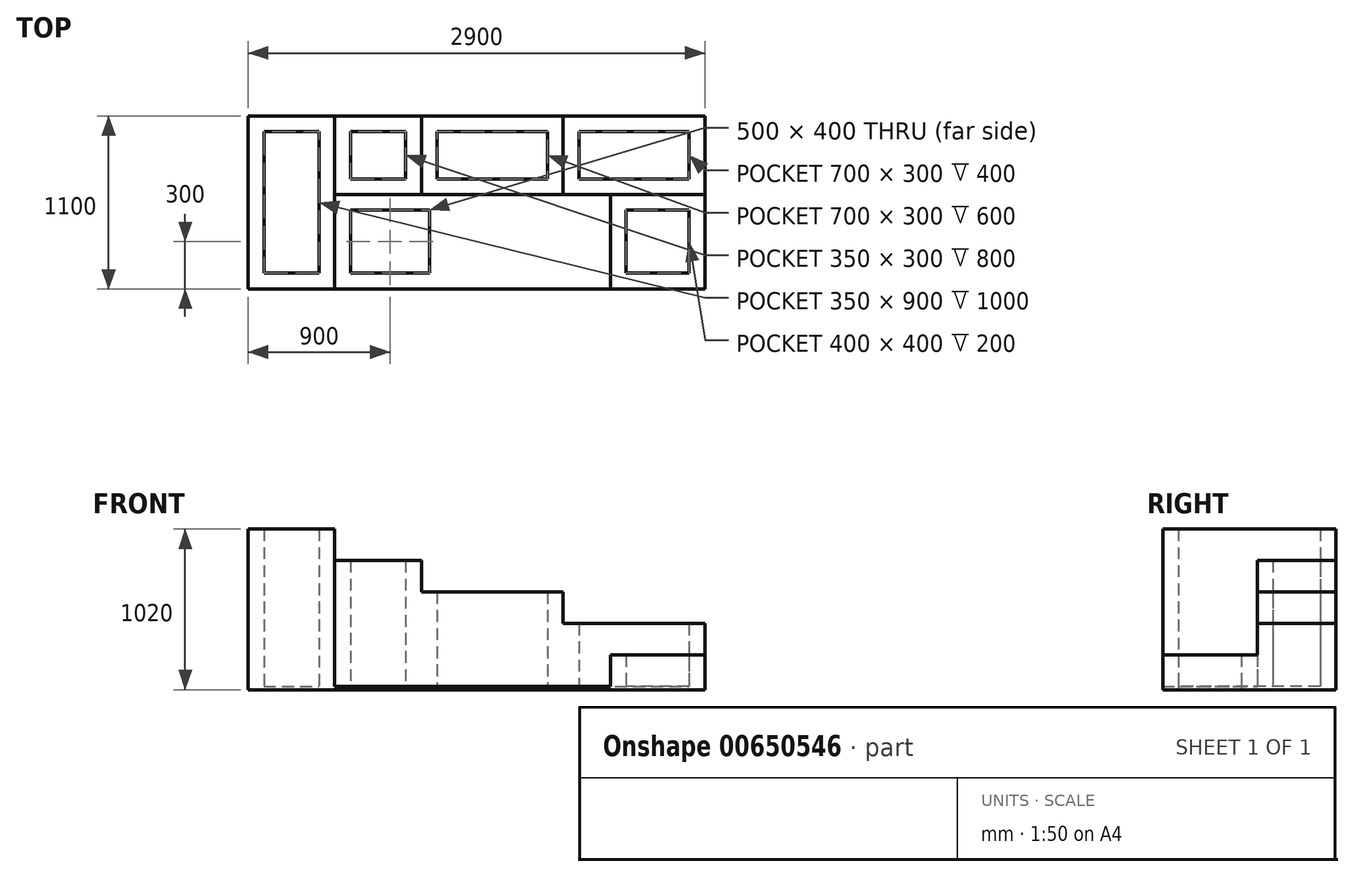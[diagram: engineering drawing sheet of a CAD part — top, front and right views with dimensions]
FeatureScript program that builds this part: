
annotation { "Feature Type Name" : "Feature", "Feature Type Description" : "" }
export const myFeature = defineFeature(function(context is Context, id is Id, definition is map)
    precondition{}
    {
        {
            var Q0;
            Q0=qCreatedBy(makeId("Top.planeOp"),FACE);
            var sketch = newSketch(context, id + "F0", { "sketchPlane" : qUnion([Q0])});
            skLineSegment(sketch, "E0.bottom", {"start": v(0, 0) * mm, "end": v(-2350, 0) * mm});
            skLineSegment(sketch, "E0.top", {"start": v(0, 1100) * mm, "end": v(-2900, 1100) * mm});
            skLineSegment(sketch, "E0.left", {"start": v(0, 0) * mm, "end": v(0, 1100) * mm});
            skLineSegment(sketch, "E0.right", {"start": v(-2900, 0) * mm, "end": v(-2900, 1100) * mm});
            skLineSegment(sketch, "E1.bottom", {"start": v(-1750, 100) * mm, "end": v(-2250, 100) * mm});
            skLineSegment(sketch, "E1.top", {"start": v(-1750, 500) * mm, "end": v(-2250, 500) * mm});
            skLineSegment(sketch, "E1.left", {"start": v(-1750, 100) * mm, "end": v(-1750, 500) * mm});
            skLineSegment(sketch, "E1.right", {"start": v(-2250, 100) * mm, "end": v(-2250, 500) * mm});
            skLineSegment(sketch, "E2", {"start": v(-2350, 0) * mm, "end": v(-2900, 0) * mm});
            skSolve(sketch);
        }
        {
            var Q0;
            Q0=makeQuery(id+"F0.imprint","IMPRINT",FACE,{"disambiguationData":[TD([[makeQuery(id+"F0.imprint","IMPRINT",EDGE,{"derivedFrom":sQuery(id+"F0.wireOp",EDGE,"E0.bottom")}),-1.0]])]});
            extrude(context, id + "F1", {"entities" : qUnion([Q0]), "depth" : 20 * mm, "offsetDistance" : 25 * mm});
        }
        {
            var Q0;
            Q0=makeQuery(id+"F1.opExtrude","CAP_FACE",FACE,{"disambiguationData":[OSD([sQuery(id+"F0.wireOp",EDGE,"E0.bottom"),sQuery(id+"F0.wireOp",EDGE,"E0.top"),sQuery(id+"F0.wireOp",EDGE,"E0.left"),sQuery(id+"F0.wireOp",EDGE,"E0.right"),sQuery(id+"F0.wireOp",EDGE,"E1.bottom"),sQuery(id+"F0.wireOp",EDGE,"E1.top"),sQuery(id+"F0.wireOp",EDGE,"E1.left"),sQuery(id+"F0.wireOp",EDGE,"E1.right")])],"isStart":false});
            var sketch = newSketch(context, id + "F2", { "sketchPlane" : qUnion([Q0])});
            skLineSegment(sketch, "E3.bottom", {"start": v(0, 1100) * mm, "end": v(-900, 1100) * mm});
            skLineSegment(sketch, "E3.top", {"start": v(0, 600) * mm, "end": v(-900, 600) * mm});
            skLineSegment(sketch, "E3.left", {"start": v(0, 1100) * mm, "end": v(0, 600) * mm});
            skLineSegment(sketch, "E3.right", {"start": v(-900, 1100) * mm, "end": v(-900, 600) * mm});
            skLineSegment(sketch, "E4.bottom", {"start": v(-800, 1000) * mm, "end": v(-100, 1000) * mm});
            skLineSegment(sketch, "E4.top", {"start": v(-800, 700) * mm, "end": v(-100, 700) * mm});
            skLineSegment(sketch, "E4.left", {"start": v(-800, 1000) * mm, "end": v(-800, 700) * mm});
            skLineSegment(sketch, "E4.right", {"start": v(-100, 1000) * mm, "end": v(-100, 700) * mm});
            skSolve(sketch);
        }
        {
            var Q0;
            Q0=qSketchRegion(id+"F2",true);
            extrude(context, id + "F3", {"entities" : qUnion([Q0]), "operationType" : NewBodyOperationType.ADD, "depth" : 400 * mm, "offsetDistance" : 25 * mm});
        }
        {
            var Q0;
            {var subQ0=sQuery(id+"F0.wireOp",EDGE,"E0.left");var subQ1=sQuery(id+"F0.wireOp",EDGE,"E1.right");var subQ2=sQuery(id+"F0.wireOp",EDGE,"E1.left");var subQ3=sQuery(id+"F0.wireOp",EDGE,"E1.top");var subQ4=sQuery(id+"F0.wireOp",EDGE,"E1.bottom");var subQ5=sQuery(id+"F0.wireOp",EDGE,"E0.bottom");var subQ6=sQuery(id+"F0.wireOp",EDGE,"E0.right");var subQ7=sQuery(id+"F0.wireOp",EDGE,"E0.top");Q0=makeQuery(id+"F3.boolean.opBoolean","SPLIT",FACE,{"disambiguationData":[TD([makeQuery(id+"F1.opExtrude","SWEPT_FACE",FACE,{"disambiguationData":[OSD([subQ5])]})])],"derivedFrom":makeQuery(id+"F1.opExtrude","CAP_FACE",FACE,{"disambiguationData":[OSD([subQ5,subQ7,subQ0,subQ6,subQ4,subQ3,subQ2,subQ1])],"isStart":false})});}
            var sketch = newSketch(context, id + "F4", { "sketchPlane" : qUnion([Q0])});
            skLineSegment(sketch, "E5.bottom", {"start": v(-900, 600) * mm, "end": v(-1800, 600) * mm});
            skLineSegment(sketch, "E5.top", {"start": v(-900, 1100) * mm, "end": v(-1800, 1100) * mm});
            skLineSegment(sketch, "E5.left", {"start": v(-900, 600) * mm, "end": v(-900, 1100) * mm});
            skLineSegment(sketch, "E5.right", {"start": v(-1800, 600) * mm, "end": v(-1800, 1100) * mm});
            skLineSegment(sketch, "E6.bottom", {"start": v(-1000, 700) * mm, "end": v(-1700, 700) * mm});
            skLineSegment(sketch, "E6.top", {"start": v(-1000, 1000) * mm, "end": v(-1700, 1000) * mm});
            skLineSegment(sketch, "E6.left", {"start": v(-1000, 700) * mm, "end": v(-1000, 1000) * mm});
            skLineSegment(sketch, "E6.right", {"start": v(-1700, 700) * mm, "end": v(-1700, 1000) * mm});
            skSolve(sketch);
        }
        {
            var Q0;
            Q0=qSketchRegion(id+"F4",true);
            extrude(context, id + "F5", {"entities" : qUnion([Q0]), "operationType" : NewBodyOperationType.ADD, "depth" : 600 * mm, "offsetDistance" : 25 * mm});
        }
        {
            var Q0;
            {var subQ1=sQuery(id+"F0.wireOp",EDGE,"E0.left");var subQ3=sQuery(id+"F0.wireOp",EDGE,"E1.right");var subQ5=sQuery(id+"F0.wireOp",EDGE,"E1.left");var subQ8=sQuery(id+"F0.wireOp",EDGE,"E1.top");var subQ11=sQuery(id+"F0.wireOp",EDGE,"E1.bottom");var subQ13=sQuery(id+"F0.wireOp",EDGE,"E0.bottom");var subQ14=makeQuery(id+"F1.opExtrude","SWEPT_FACE",FACE,{"disambiguationData":[OSD([subQ13])]});var subQ15=sQuery(id+"F0.wireOp",EDGE,"E0.right");var subQ17=sQuery(id+"F0.wireOp",EDGE,"E0.top");Q0=makeQuery(id+"F5.boolean.opBoolean","SPLIT",FACE,{"disambiguationData":[TD([subQ14])],"derivedFrom":makeQuery(id+"F3.boolean.opBoolean","SPLIT",FACE,{"disambiguationData":[TD([subQ14])],"derivedFrom":makeQuery(id+"F1.opExtrude","CAP_FACE",FACE,{"disambiguationData":[OSD([subQ13,subQ17,subQ1,subQ15,subQ11,subQ8,subQ5,subQ3])],"isStart":false})})});}
            var sketch = newSketch(context, id + "F6", { "sketchPlane" : qUnion([Q0])});
            skLineSegment(sketch, "E7.bottom", {"start": v(-1800, 600) * mm, "end": v(-2350, 600) * mm});
            skLineSegment(sketch, "E7.top", {"start": v(-1800, 1100) * mm, "end": v(-2350, 1100) * mm});
            skLineSegment(sketch, "E7.left", {"start": v(-1800, 600) * mm, "end": v(-1800, 1100) * mm});
            skLineSegment(sketch, "E7.right", {"start": v(-2350, 600) * mm, "end": v(-2350, 1100) * mm});
            skLineSegment(sketch, "E8.bottom", {"start": v(-1900, 700) * mm, "end": v(-2250, 700) * mm});
            skLineSegment(sketch, "E8.top", {"start": v(-1900, 1000) * mm, "end": v(-2250, 1000) * mm});
            skLineSegment(sketch, "E8.left", {"start": v(-1900, 700) * mm, "end": v(-1900, 1000) * mm});
            skLineSegment(sketch, "E8.right", {"start": v(-2250, 700) * mm, "end": v(-2250, 1000) * mm});
            skSolve(sketch);
        }
        {
            var Q0;
            Q0=qSketchRegion(id+"F6",true);
            extrude(context, id + "F7", {"entities" : qUnion([Q0]), "operationType" : NewBodyOperationType.ADD, "depth" : 800 * mm, "offsetDistance" : 25 * mm});
        }
        {
            var Q0;
            {var subQ1=sQuery(id+"F0.wireOp",EDGE,"E0.left");var subQ3=sQuery(id+"F0.wireOp",EDGE,"E1.right");var subQ5=sQuery(id+"F0.wireOp",EDGE,"E1.left");var subQ8=sQuery(id+"F0.wireOp",EDGE,"E1.top");var subQ11=sQuery(id+"F0.wireOp",EDGE,"E1.bottom");var subQ13=sQuery(id+"F0.wireOp",EDGE,"E0.bottom");var subQ14=makeQuery(id+"F1.opExtrude","SWEPT_FACE",FACE,{"disambiguationData":[OSD([subQ13])]});var subQ15=sQuery(id+"F0.wireOp",EDGE,"E0.right");var subQ17=sQuery(id+"F0.wireOp",EDGE,"E0.top");Q0=makeQuery(id+"F7.boolean.opBoolean","SPLIT",FACE,{"disambiguationData":[TD([subQ14])],"derivedFrom":makeQuery(id+"F5.boolean.opBoolean","SPLIT",FACE,{"disambiguationData":[TD([subQ14])],"derivedFrom":makeQuery(id+"F3.boolean.opBoolean","SPLIT",FACE,{"disambiguationData":[TD([subQ14])],"derivedFrom":makeQuery(id+"F1.opExtrude","CAP_FACE",FACE,{"disambiguationData":[OSD([subQ13,subQ17,subQ1,subQ15,subQ11,subQ8,subQ5,subQ3])],"isStart":false})})})});}
            var sketch = newSketch(context, id + "F8", { "sketchPlane" : qUnion([Q0])});
            skLineSegment(sketch, "E9.bottom", {"start": v(-2900, 1100) * mm, "end": v(-2350, 1100) * mm});
            skLineSegment(sketch, "E9.top", {"start": v(-2900, 0) * mm, "end": v(-2350, 0) * mm});
            skLineSegment(sketch, "E9.left", {"start": v(-2900, 1100) * mm, "end": v(-2900, 0) * mm});
            skLineSegment(sketch, "E9.right", {"start": v(-2350, 1100) * mm, "end": v(-2350, 0) * mm});
            skLineSegment(sketch, "E10.bottom", {"start": v(-2800, 1000) * mm, "end": v(-2450, 1000) * mm});
            skLineSegment(sketch, "E10.top", {"start": v(-2800, 100) * mm, "end": v(-2450, 100) * mm});
            skLineSegment(sketch, "E10.left", {"start": v(-2800, 1000) * mm, "end": v(-2800, 100) * mm});
            skLineSegment(sketch, "E10.right", {"start": v(-2450, 1000) * mm, "end": v(-2450, 100) * mm});
            skSolve(sketch);
        }
        {
            var Q0;
            Q0=qSketchRegion(id+"F8",true);
            extrude(context, id + "F9", {"entities" : qUnion([Q0]), "operationType" : NewBodyOperationType.ADD, "depth" : 1000 * mm, "offsetDistance" : 25 * mm});
        }
        {
            var Q0;
            {var subQ1=sQuery(id+"F0.wireOp",EDGE,"E1.top");var subQ5=sQuery(id+"F0.wireOp",EDGE,"E1.left");var subQ7=sQuery(id+"F0.wireOp",EDGE,"E1.right");var subQ9=sQuery(id+"F0.wireOp",EDGE,"E2");var subQ10=sQuery(id+"F0.wireOp",EDGE,"E0.bottom");var subQ12=sQuery(id+"F0.wireOp",EDGE,"E0.left");var subQ13=makeQuery(id+"F1.opExtrude","SWEPT_FACE",FACE,{"disambiguationData":[OSD([subQ12])]});var subQ15=sQuery(id+"F0.wireOp",EDGE,"E1.bottom");var subQ18=sQuery(id+"F0.wireOp",EDGE,"E0.top");var subQ19=makeQuery(id+"F1.opExtrude","SWEPT_FACE",FACE,{"disambiguationData":[OSD([subQ18])]});var subQ20=sQuery(id+"F0.wireOp",EDGE,"E0.right");Q0=makeQuery(id+"F9.boolean.opBoolean","SPLIT",FACE,{"disambiguationData":[TD([subQ13])],"derivedFrom":makeQuery(id+"F7.boolean.opBoolean","SPLIT",FACE,{"disambiguationData":[TD([subQ19])],"derivedFrom":makeQuery(id+"F5.boolean.opBoolean","SPLIT",FACE,{"disambiguationData":[TD([subQ19])],"derivedFrom":makeQuery(id+"F3.boolean.opBoolean","SPLIT",FACE,{"disambiguationData":[TD([subQ19])],"derivedFrom":makeQuery(id+"F1.opExtrude","CAP_FACE",FACE,{"disambiguationData":[OSD([subQ10,subQ18,subQ12,subQ20,subQ15,subQ1,subQ5,subQ7,subQ9])],"isStart":false})})})})});}
            var sketch = newSketch(context, id + "F10", { "sketchPlane" : qUnion([Q0])});
            skLineSegment(sketch, "E11.bottom", {"start": v(0, 0) * mm, "end": v(-600, 0) * mm});
            skLineSegment(sketch, "E11.top", {"start": v(0, 600) * mm, "end": v(-600, 600) * mm});
            skLineSegment(sketch, "E11.left", {"start": v(0, 0) * mm, "end": v(0, 600) * mm});
            skLineSegment(sketch, "E11.right", {"start": v(-600, 0) * mm, "end": v(-600, 600) * mm});
            skLineSegment(sketch, "E12.bottom", {"start": v(-100, 100) * mm, "end": v(-500, 100) * mm});
            skLineSegment(sketch, "E12.top", {"start": v(-100, 500) * mm, "end": v(-500, 500) * mm});
            skLineSegment(sketch, "E12.left", {"start": v(-100, 100) * mm, "end": v(-100, 500) * mm});
            skLineSegment(sketch, "E12.right", {"start": v(-500, 100) * mm, "end": v(-500, 500) * mm});
            skSolve(sketch);
        }
        {
            var Q0;
            Q0=qSketchRegion(id+"F10",true);
            extrude(context, id + "F11", {"entities" : qUnion([Q0]), "operationType" : NewBodyOperationType.ADD, "depth" : 200 * mm, "offsetDistance" : 25 * mm});
        }
    });
